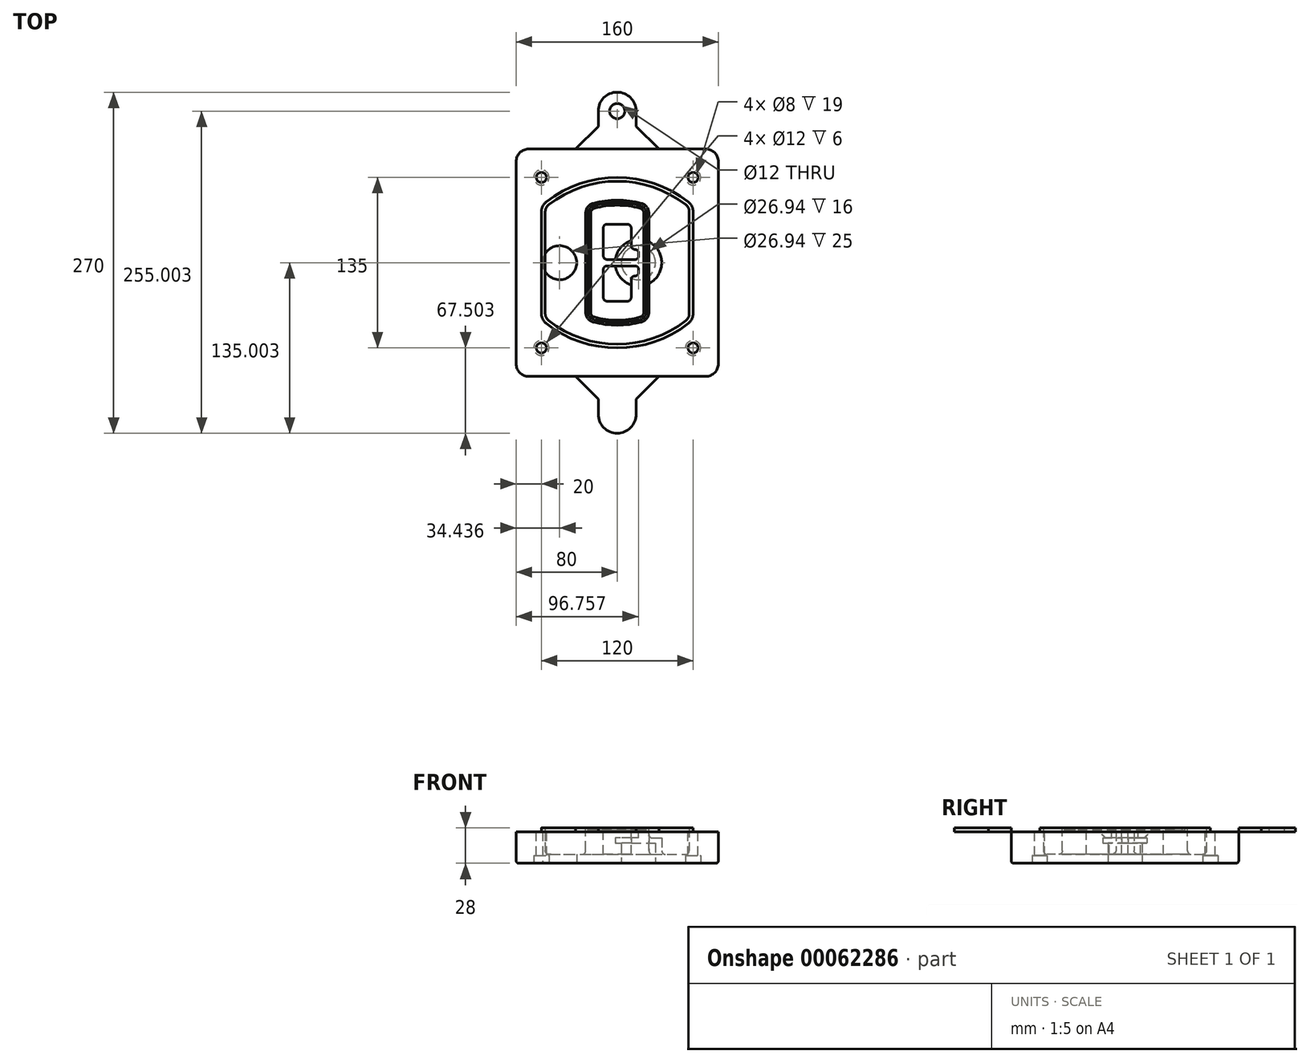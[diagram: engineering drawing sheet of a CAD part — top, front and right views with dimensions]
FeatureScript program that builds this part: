
annotation { "Feature Type Name" : "Feature", "Feature Type Description" : "" }
export const myFeature = defineFeature(function(context is Context, id is Id, definition is map)
    precondition{}
    {
        {
            var Q0;
            Q0=qCreatedBy(makeId("Top.planeOp"),FACE);
            var sketch = newSketch(context, id + "F0", { "sketchPlane" : qUnion([Q0])});
            skPoint(sketch, "E0.rect.middle", {"position": v(0, 0) * mm});
            skLineSegment(sketch, "E1.bottom", {"start": v(24.05, 28.38) * mm, "end": v(164.05, 28.38) * mm});
            skLineSegment(sketch, "E1.top", {"start": v(24.05, 208.38) * mm, "end": v(164.05, 208.38) * mm});
            skLineSegment(sketch, "E1.left", {"start": v(14.05, 38.38) * mm, "end": v(14.05, 198.38) * mm});
            skLineSegment(sketch, "E1.right", {"start": v(174.05, 38.38) * mm, "end": v(174.05, 198.38) * mm});
            skLineSegment(sketch, "E2", {"start": v(14.05, 208.38) * mm, "end": v(174.05, 28.38) * mm, "construction": true});
            skLineSegment(sketch, "E3", {"start": v(174.05, 208.38) * mm, "end": v(14.05, 28.38) * mm, "construction": true});
            skCircle(sketch, "E4", {"center": v(34.05, 185.88) * mm, "radius": 4 * mm});
            skCircle(sketch, "E5", {"center": v(154.05, 185.88) * mm, "radius": 4 * mm});
            skCircle(sketch, "E6", {"center": v(154.05, 50.88) * mm, "radius": 4 * mm});
            skCircle(sketch, "E7", {"center": v(34.05, 50.88) * mm, "radius": 4 * mm});
            skLineSegment(sketch, "E8", {"start": v(34.05, 185.88) * mm, "end": v(154.05, 185.88) * mm, "construction": true});
            skLineSegment(sketch, "E9", {"start": v(154.05, 185.88) * mm, "end": v(154.05, 50.88) * mm, "construction": true});
            skLineSegment(sketch, "E10", {"start": v(154.05, 50.88) * mm, "end": v(34.05, 50.88) * mm, "construction": true});
            skLineSegment(sketch, "E11", {"start": v(34.05, 50.88) * mm, "end": v(34.05, 185.88) * mm, "construction": true});
            skLineSegment(sketch, "E12", {"start": v(34.05, 158.68) * mm, "end": v(34.05, 78.09) * mm});
            skLineSegment(sketch, "E13", {"start": v(154.05, 158.68) * mm, "end": v(154.05, 78.09) * mm});
            skArc(sketch, "E14", {"start": v(150.2, 166.56) * mm, "mid": v(94.05, 185.88) * mm, "end": v(37.9, 166.56) * mm});
            skArc(sketch, "E15", {"start": v(37.9, 70.2) * mm, "mid": v(94.05, 50.88) * mm, "end": v(150.2, 70.2) * mm});
            skLineSegment(sketch, "E16", {"start": v(34.05, 118.38) * mm, "end": v(154.05, 118.38) * mm, "construction": true});
            skPoint(sketch, "E17.visualSharp", {"position": v(34.05, 73.38) * mm});
            skArc(sketch, "E17.filletArc", {"start": v(34.05, 78.09) * mm, "mid": v(35.06, 73.7) * mm, "end": v(37.9, 70.2) * mm});
            skPoint(sketch, "E18.visualSharp", {"position": v(34.05, 163.38) * mm});
            skArc(sketch, "E18.filletArc", {"start": v(37.9, 166.56) * mm, "mid": v(35.06, 163.06) * mm, "end": v(34.05, 158.68) * mm});
            skPoint(sketch, "E19.visualSharp", {"position": v(154.05, 163.38) * mm});
            skArc(sketch, "E19.filletArc", {"start": v(154.05, 158.68) * mm, "mid": v(153.04, 163.06) * mm, "end": v(150.2, 166.56) * mm});
            skPoint(sketch, "E20.visualSharp", {"position": v(154.05, 73.38) * mm});
            skArc(sketch, "E20.filletArc", {"start": v(150.2, 70.2) * mm, "mid": v(153.04, 73.7) * mm, "end": v(154.05, 78.09) * mm});
            skPoint(sketch, "E21.visualSharp", {"position": v(14.05, 208.38) * mm});
            skArc(sketch, "E21.filletArc", {"start": v(24.05, 208.38) * mm, "mid": v(16.98, 205.45) * mm, "end": v(14.05, 198.38) * mm});
            skPoint(sketch, "E22.visualSharp", {"position": v(174.05, 208.38) * mm});
            skArc(sketch, "E22.filletArc", {"start": v(174.05, 198.38) * mm, "mid": v(171.12, 205.45) * mm, "end": v(164.05, 208.38) * mm});
            skPoint(sketch, "E23.visualSharp", {"position": v(174.05, 28.38) * mm});
            skArc(sketch, "E23.filletArc", {"start": v(164.05, 28.38) * mm, "mid": v(171.12, 31.31) * mm, "end": v(174.05, 38.38) * mm});
            skPoint(sketch, "E24.visualSharp", {"position": v(14.05, 28.38) * mm});
            skArc(sketch, "E24.filletArc", {"start": v(14.05, 38.38) * mm, "mid": v(16.98, 31.31) * mm, "end": v(24.05, 28.38) * mm});
            skArc(sketch, "E25.0", {"start": v(151.05, 158.68) * mm, "mid": v(150.34, 161.75) * mm, "end": v(148.36, 164.2) * mm});
            skLineSegment(sketch, "E25.1", {"start": v(151.05, 158.68) * mm, "end": v(151.05, 78.09) * mm});
            skArc(sketch, "E25.2", {"start": v(148.36, 72.57) * mm, "mid": v(150.34, 75.02) * mm, "end": v(151.05, 78.09) * mm});
            skArc(sketch, "E25.3", {"start": v(39.74, 72.57) * mm, "mid": v(94.05, 53.88) * mm, "end": v(148.36, 72.57) * mm});
            skArc(sketch, "E25.4", {"start": v(37.05, 78.09) * mm, "mid": v(37.76, 75.02) * mm, "end": v(39.74, 72.57) * mm});
            skArc(sketch, "E25.5", {"start": v(148.36, 164.2) * mm, "mid": v(94.05, 182.88) * mm, "end": v(39.74, 164.2) * mm});
            skLineSegment(sketch, "E25.6", {"start": v(37.05, 158.68) * mm, "end": v(37.05, 78.09) * mm});
            skArc(sketch, "E25.7", {"start": v(39.74, 164.2) * mm, "mid": v(37.76, 161.75) * mm, "end": v(37.05, 158.68) * mm});
            skArc(sketch, "E26.0", {"start": v(35.43, 169.71) * mm, "mid": v(31.47, 164.82) * mm, "end": v(30.05, 158.68) * mm});
            skArc(sketch, "E26.1", {"start": v(152.67, 169.71) * mm, "mid": v(94.05, 189.88) * mm, "end": v(35.43, 169.71) * mm});
            skArc(sketch, "E26.2", {"start": v(158.05, 158.68) * mm, "mid": v(156.63, 164.82) * mm, "end": v(152.67, 169.71) * mm});
            skLineSegment(sketch, "E26.3", {"start": v(158.05, 158.68) * mm, "end": v(158.05, 78.09) * mm});
            skArc(sketch, "E26.4", {"start": v(152.67, 67.05) * mm, "mid": v(156.63, 71.95) * mm, "end": v(158.05, 78.09) * mm});
            skLineSegment(sketch, "E26.5", {"start": v(30.05, 158.68) * mm, "end": v(30.05, 78.09) * mm});
            skArc(sketch, "E26.6", {"start": v(35.43, 67.05) * mm, "mid": v(94.05, 46.88) * mm, "end": v(152.67, 67.05) * mm});
            skArc(sketch, "E26.7", {"start": v(30.05, 78.09) * mm, "mid": v(31.47, 71.95) * mm, "end": v(35.43, 67.05) * mm});
            skSolve(sketch);
        }
        {
            var Q0;
            Q0=makeQuery(id+"F0.imprint","IMPRINT",FACE,{"disambiguationData":[TD([[makeQuery(id+"F0.imprint","IMPRINT",EDGE,{"derivedFrom":sQuery(id+"F0.wireOp",EDGE,"E1.bottom")}),1.0]])]});
            var Q1;
            Q1=makeQuery(id+"F0.imprint","IMPRINT",FACE,{"disambiguationData":[TD([[makeQuery(id+"F0.imprint","IMPRINT",EDGE,{"derivedFrom":sQuery(id+"F0.wireOp",EDGE,"E12")}),1.0]])]});
            var Q2;
            Q2=makeQuery(id+"F0.imprint","IMPRINT",FACE,{"disambiguationData":[TD([[makeQuery(id+"F0.imprint","IMPRINT",EDGE,{"derivedFrom":sQuery(id+"F0.wireOp",EDGE,"E25.0")}),1.0]])]});
            var Q3;
            Q3=makeQuery(id+"F0.imprint","IMPRINT",FACE,{"disambiguationData":[TD([[makeQuery(id+"F0.imprint","IMPRINT",EDGE,{"derivedFrom":sQuery(id+"F0.wireOp",EDGE,"E12")}),-1.0]])]});
            extrude(context, id + "F1", {"entities" : qUnion([Q0, Q1, Q2, Q3]), "oppositeDirection" : true, "depth" : 25 * mm});
        }
        {
            var Q0;
            Q0=makeQuery(id+"F0.imprint","IMPRINT",FACE,{"disambiguationData":[TD([[makeQuery(id+"F0.imprint","IMPRINT",EDGE,{"derivedFrom":sQuery(id+"F0.wireOp",EDGE,"E12")}),1.0]])]});
            extrude(context, id + "F2", {"entities" : qUnion([Q0]), "operationType" : NewBodyOperationType.ADD, "depth" : 3 * mm});
        }
        {
            var Q0;
            Q0=makeQuery(id+"F0.imprint","IMPRINT",FACE,{"disambiguationData":[TD([[makeQuery(id+"F0.imprint","IMPRINT",EDGE,{"derivedFrom":sQuery(id+"F0.wireOp",EDGE,"E25.0")}),1.0]])]});
            extrude(context, id + "F3", {"entities" : qUnion([Q0]), "operationType" : NewBodyOperationType.REMOVE, "oppositeDirection" : true, "depth" : 18 * mm});
        }
        {
            var Q0;
            Q0=makeQuery(id+"F2.opExtrude","CAP_FACE",FACE,{"disambiguationData":[OSD([sQuery(id+"F0.wireOp",EDGE,"E12"),sQuery(id+"F0.wireOp",EDGE,"E13"),sQuery(id+"F0.wireOp",EDGE,"E14"),sQuery(id+"F0.wireOp",EDGE,"E15"),sQuery(id+"F0.wireOp",EDGE,"E17.filletArc"),sQuery(id+"F0.wireOp",EDGE,"E18.filletArc"),sQuery(id+"F0.wireOp",EDGE,"E19.filletArc"),sQuery(id+"F0.wireOp",EDGE,"E20.filletArc"),sQuery(id+"F0.wireOp",EDGE,"E25.0"),sQuery(id+"F0.wireOp",EDGE,"E25.1"),sQuery(id+"F0.wireOp",EDGE,"E25.2"),sQuery(id+"F0.wireOp",EDGE,"E25.3"),sQuery(id+"F0.wireOp",EDGE,"E25.4"),sQuery(id+"F0.wireOp",EDGE,"E25.5"),sQuery(id+"F0.wireOp",EDGE,"E25.6"),sQuery(id+"F0.wireOp",EDGE,"E25.7")])],"isStart":false});
            var sketch = newSketch(context, id + "F4", { "sketchPlane" : qUnion([Q0])});
            skArc(sketch, "E27.0", {"start": v(74.97, 71.41) * mm, "mid": v(94.05, 68.88) * mm, "end": v(113.13, 71.41) * mm});
            skArc(sketch, "E28.0", {"start": v(113.13, 165.35) * mm, "mid": v(94.05, 167.88) * mm, "end": v(74.97, 165.35) * mm});
            skLineSegment(sketch, "E29", {"start": v(69.05, 157.63) * mm, "end": v(69.05, 79.14) * mm});
            skLineSegment(sketch, "E30", {"start": v(119.05, 157.63) * mm, "end": v(119.05, 79.14) * mm});
            skLineSegment(sketch, "E31", {"start": v(69.05, 163.48) * mm, "end": v(119.05, 163.48) * mm, "construction": true});
            skLineSegment(sketch, "E32", {"start": v(69.05, 73.28) * mm, "end": v(119.05, 73.28) * mm, "construction": true});
            skPoint(sketch, "E33.visualSharp", {"position": v(69.05, 163.48) * mm});
            skArc(sketch, "E33.filletArc", {"start": v(74.97, 165.35) * mm, "mid": v(70.7, 162.5) * mm, "end": v(69.05, 157.63) * mm});
            skPoint(sketch, "E34.visualSharp", {"position": v(119.05, 163.48) * mm});
            skArc(sketch, "E34.filletArc", {"start": v(119.05, 157.63) * mm, "mid": v(117.4, 162.5) * mm, "end": v(113.13, 165.35) * mm});
            skPoint(sketch, "E35.visualSharp", {"position": v(119.05, 73.28) * mm});
            skArc(sketch, "E35.filletArc", {"start": v(113.13, 71.41) * mm, "mid": v(117.4, 74.27) * mm, "end": v(119.05, 79.14) * mm});
            skPoint(sketch, "E36.visualSharp", {"position": v(69.05, 73.28) * mm});
            skArc(sketch, "E36.filletArc", {"start": v(69.05, 79.14) * mm, "mid": v(70.7, 74.27) * mm, "end": v(74.97, 71.41) * mm});
            skArc(sketch, "E37.0", {"start": v(148.36, 164.2) * mm, "mid": v(94.05, 182.88) * mm, "end": v(39.74, 164.2) * mm});
            skArc(sketch, "E37.1", {"start": v(39.74, 164.2) * mm, "mid": v(37.76, 161.75) * mm, "end": v(37.05, 158.68) * mm});
            skLineSegment(sketch, "E37.2", {"start": v(37.05, 158.68) * mm, "end": v(37.05, 78.09) * mm});
            skArc(sketch, "E37.3", {"start": v(37.05, 78.09) * mm, "mid": v(37.76, 75.02) * mm, "end": v(39.74, 72.57) * mm});
            skArc(sketch, "E37.4", {"start": v(39.74, 72.57) * mm, "mid": v(94.05, 53.88) * mm, "end": v(148.36, 72.57) * mm});
            skArc(sketch, "E37.5", {"start": v(148.36, 72.57) * mm, "mid": v(150.34, 75.02) * mm, "end": v(151.05, 78.09) * mm});
            skLineSegment(sketch, "E37.6", {"start": v(151.05, 158.68) * mm, "end": v(151.05, 78.09) * mm});
            skArc(sketch, "E37.7", {"start": v(151.05, 158.68) * mm, "mid": v(150.34, 161.75) * mm, "end": v(148.36, 164.2) * mm});
            skLineSegment(sketch, "E38.0", {"start": v(117.05, 157.63) * mm, "end": v(117.05, 79.14) * mm});
            skArc(sketch, "E38.1", {"start": v(112.61, 73.34) * mm, "mid": v(115.81, 75.49) * mm, "end": v(117.05, 79.14) * mm});
            skArc(sketch, "E38.2", {"start": v(75.49, 73.34) * mm, "mid": v(94.05, 70.88) * mm, "end": v(112.61, 73.34) * mm});
            skArc(sketch, "E38.3", {"start": v(71.05, 79.14) * mm, "mid": v(72.29, 75.49) * mm, "end": v(75.49, 73.34) * mm});
            skLineSegment(sketch, "E38.4", {"start": v(71.05, 157.63) * mm, "end": v(71.05, 79.14) * mm});
            skArc(sketch, "E38.5", {"start": v(117.05, 157.63) * mm, "mid": v(115.81, 161.28) * mm, "end": v(112.61, 163.42) * mm});
            skArc(sketch, "E38.6", {"start": v(75.49, 163.42) * mm, "mid": v(72.29, 161.28) * mm, "end": v(71.05, 157.63) * mm});
            skArc(sketch, "E38.7", {"start": v(112.61, 163.42) * mm, "mid": v(94.05, 165.88) * mm, "end": v(75.49, 163.42) * mm});
            skArc(sketch, "E39.0", {"start": v(115.05, 157.63) * mm, "mid": v(114.23, 160.06) * mm, "end": v(112.1, 161.5) * mm});
            skLineSegment(sketch, "E39.1", {"start": v(115.05, 157.63) * mm, "end": v(115.05, 79.14) * mm});
            skArc(sketch, "E39.2", {"start": v(112.1, 75.27) * mm, "mid": v(114.23, 76.7) * mm, "end": v(115.05, 79.14) * mm});
            skArc(sketch, "E39.3", {"start": v(76, 75.27) * mm, "mid": v(94.05, 72.88) * mm, "end": v(112.1, 75.27) * mm});
            skArc(sketch, "E39.4", {"start": v(73.05, 79.14) * mm, "mid": v(73.87, 76.7) * mm, "end": v(76, 75.27) * mm});
            skArc(sketch, "E39.5", {"start": v(112.1, 161.5) * mm, "mid": v(94.05, 163.88) * mm, "end": v(76, 161.5) * mm});
            skLineSegment(sketch, "E39.6", {"start": v(73.05, 157.63) * mm, "end": v(73.05, 79.14) * mm});
            skArc(sketch, "E39.7", {"start": v(76, 161.5) * mm, "mid": v(73.87, 160.06) * mm, "end": v(73.05, 157.63) * mm});
            skLineSegment(sketch, "E40", {"start": v(69.05, 118.38) * mm, "end": v(119.05, 118.38) * mm, "construction": true});
            skLineSegment(sketch, "E41", {"start": v(83.05, 123.88) * mm, "end": v(83.05, 145.88) * mm});
            skLineSegment(sketch, "E42", {"start": v(86.05, 148.88) * mm, "end": v(102.05, 148.88) * mm});
            skLineSegment(sketch, "E43", {"start": v(105.05, 145.88) * mm, "end": v(105.05, 131.88) * mm});
            skLineSegment(sketch, "E44", {"start": v(108.05, 128.88) * mm, "end": v(108.05, 128.88) * mm});
            skLineSegment(sketch, "E45", {"start": v(111.05, 125.88) * mm, "end": v(111.05, 123.88) * mm});
            skLineSegment(sketch, "E46", {"start": v(108.05, 120.88) * mm, "end": v(86.05, 120.88) * mm});
            skPoint(sketch, "E47.visualSharp", {"position": v(83.05, 148.88) * mm});
            skArc(sketch, "E47.filletArc", {"start": v(86.05, 148.88) * mm, "mid": v(83.93, 148) * mm, "end": v(83.05, 145.88) * mm});
            skPoint(sketch, "E48.visualSharp", {"position": v(105.05, 148.88) * mm});
            skArc(sketch, "E48.filletArc", {"start": v(105.05, 145.88) * mm, "mid": v(104.17, 148) * mm, "end": v(102.05, 148.88) * mm});
            skPoint(sketch, "E49.visualSharp", {"position": v(105.05, 128.88) * mm});
            skArc(sketch, "E49.filletArc", {"start": v(105.05, 131.88) * mm, "mid": v(105.93, 129.76) * mm, "end": v(108.05, 128.88) * mm});
            skPoint(sketch, "E50.visualSharp", {"position": v(111.05, 128.88) * mm});
            skArc(sketch, "E50.filletArc", {"start": v(111.05, 125.88) * mm, "mid": v(110.17, 128) * mm, "end": v(108.05, 128.88) * mm});
            skPoint(sketch, "E51.visualSharp", {"position": v(111.05, 120.88) * mm});
            skArc(sketch, "E51.filletArc", {"start": v(108.05, 120.88) * mm, "mid": v(110.17, 121.76) * mm, "end": v(111.05, 123.88) * mm});
            skPoint(sketch, "E52.visualSharp", {"position": v(83.05, 120.88) * mm});
            skArc(sketch, "E52.filletArc", {"start": v(83.05, 123.88) * mm, "mid": v(83.93, 121.76) * mm, "end": v(86.05, 120.88) * mm});
            skLineSegment(sketch, "E53.0.MirrorCS", {"start": v(108.05, 115.88) * mm, "end": v(86.05, 115.88) * mm});
            skArc(sketch, "E54.0.MirrorCS", {"start": v(83.05, 112.88) * mm, "mid": v(83.93, 115) * mm, "end": v(86.05, 115.88) * mm});
            skLineSegment(sketch, "E55.0.MirrorCS", {"start": v(83.05, 112.88) * mm, "end": v(83.05, 90.88) * mm});
            skArc(sketch, "E56.0.MirrorCS", {"start": v(86.05, 87.88) * mm, "mid": v(83.93, 88.76) * mm, "end": v(83.05, 90.88) * mm});
            skLineSegment(sketch, "E57.0.MirrorCS", {"start": v(86.05, 87.88) * mm, "end": v(102.05, 87.88) * mm});
            skArc(sketch, "E58.0.MirrorCS", {"start": v(105.05, 90.88) * mm, "mid": v(104.17, 88.76) * mm, "end": v(102.05, 87.88) * mm});
            skLineSegment(sketch, "E59.0.MirrorCS", {"start": v(105.05, 90.88) * mm, "end": v(105.05, 104.88) * mm});
            skArc(sketch, "E60.0.MirrorCS", {"start": v(105.05, 104.88) * mm, "mid": v(105.93, 107) * mm, "end": v(108.05, 107.88) * mm});
            skArc(sketch, "E61.0.MirrorCS", {"start": v(111.05, 110.88) * mm, "mid": v(110.17, 108.76) * mm, "end": v(108.05, 107.88) * mm});
            skLineSegment(sketch, "E62.0.MirrorCS", {"start": v(111.05, 110.88) * mm, "end": v(111.05, 112.88) * mm});
            skArc(sketch, "E63.0.MirrorCS", {"start": v(108.05, 115.88) * mm, "mid": v(110.17, 115) * mm, "end": v(111.05, 112.88) * mm});
            skSolve(sketch);
        }
        {
            var Q0;
            Q0=makeQuery(id+"F4.imprint","IMPRINT",FACE,{"disambiguationData":[TD([[makeQuery(id+"F4.imprint","IMPRINT",EDGE,{"derivedFrom":sQuery(id+"F4.wireOp",EDGE,"E27.0")}),1.0]])]});
            var Q1;
            Q1=makeQuery(id+"F4.imprint","IMPRINT",FACE,{"disambiguationData":[TD([[makeQuery(id+"F4.imprint","IMPRINT",EDGE,{"derivedFrom":sQuery(id+"F4.wireOp",EDGE,"E38.0")}),-1.0]])]});
            var Q2;
            Q2=makeQuery(id+"F4.imprint","IMPRINT",FACE,{"disambiguationData":[TD([[makeQuery(id+"F4.imprint","IMPRINT",EDGE,{"derivedFrom":sQuery(id+"F4.wireOp",EDGE,"E39.0")}),1.0]])]});
            extrude(context, id + "F5", {"entities" : qUnion([Q0, Q1, Q2]), "operationType" : NewBodyOperationType.ADD, "endBound" : BoundingType.UP_TO_NEXT, "oppositeDirection" : true, "depth" : 25 * mm});
        }
        {
            var Q0;
            Q0=makeQuery(id+"F4.imprint","IMPRINT",FACE,{"disambiguationData":[TD([[makeQuery(id+"F4.imprint","IMPRINT",EDGE,{"derivedFrom":sQuery(id+"F4.wireOp",EDGE,"E38.0")}),-1.0]])]});
            extrude(context, id + "F6", {"entities" : qUnion([Q0]), "operationType" : NewBodyOperationType.REMOVE, "oppositeDirection" : true, "depth" : 2 * mm});
        }
        {
            var Q0;
            Q0=makeQuery(id+"F1.opExtrude","CAP_FACE",FACE,{"disambiguationData":[OSD([sQuery(id+"F0.wireOp",EDGE,"E1.bottom"),sQuery(id+"F0.wireOp",EDGE,"E1.top"),sQuery(id+"F0.wireOp",EDGE,"E1.left"),sQuery(id+"F0.wireOp",EDGE,"E1.right"),sQuery(id+"F0.wireOp",EDGE,"E4"),sQuery(id+"F0.wireOp",EDGE,"E5"),sQuery(id+"F0.wireOp",EDGE,"E6"),sQuery(id+"F0.wireOp",EDGE,"E7"),sQuery(id+"F0.wireOp",EDGE,"E21.filletArc"),sQuery(id+"F0.wireOp",EDGE,"E22.filletArc"),sQuery(id+"F0.wireOp",EDGE,"E23.filletArc"),sQuery(id+"F0.wireOp",EDGE,"E24.filletArc")])],"isStart":false});
            var sketch = newSketch(context, id + "F7", { "sketchPlane" : qUnion([Q0])});
            skCircle(sketch, "E64", {"center": v(110.8, -118.38) * mm, "radius": 13.47 * mm});
            skCircle(sketch, "E65", {"center": v(48.49, -118.38) * mm, "radius": 13.47 * mm});
            skLineSegment(sketch, "E66", {"start": v(174.05, -118.38) * mm, "end": v(14.05, -118.38) * mm});
            skCircle(sketch, "E67", {"center": v(110.8, -118.38) * mm, "radius": 18.47 * mm});
            skCircle(sketch, "E68", {"center": v(154.05, -185.88) * mm, "radius": 6 * mm});
            skCircle(sketch, "E69", {"center": v(34.05, -185.88) * mm, "radius": 6 * mm});
            skCircle(sketch, "E70", {"center": v(34.05, -50.88) * mm, "radius": 6 * mm});
            skCircle(sketch, "E71", {"center": v(154.05, -50.88) * mm, "radius": 6 * mm});
            skSolve(sketch);
        }
        {
            var Q0;
            {var subQ1=sQuery(id+"F7.wireOp",EDGE,"E66");var subQ4=sQuery(id+"F7.wireOp",EDGE,"E64");var subQ6=makeQuery(id+"F7.imprint","INTERSECT",VERTEX,{"disambiguationData":[OD(0.0)],"derivedFrom":[subQ4,subQ1]});Q0=makeQuery(id+"F7.imprint","IMPRINT",FACE,{"disambiguationData":[TD([[makeQuery(id+"F7.imprint","IMPRINT",EDGE,{"disambiguationData":[TD([[subQ6,-1.0]])],"derivedFrom":subQ4}),-1.0]])]});}
            var Q1;
            {var subQ0=sQuery(id+"F7.wireOp",EDGE,"E66");var subQ1=sQuery(id+"F7.wireOp",EDGE,"E64");var subQ3=makeQuery(id+"F7.imprint","INTERSECT",VERTEX,{"disambiguationData":[OD(0.0)],"derivedFrom":[subQ1,subQ0]});Q1=makeQuery(id+"F7.imprint","IMPRINT",FACE,{"disambiguationData":[TD([[makeQuery(id+"F7.imprint","IMPRINT",EDGE,{"disambiguationData":[TD([[subQ3,-1.0]])],"derivedFrom":subQ1}),1.0]])]});}
            var Q2;
            {var subQ0=sQuery(id+"F7.wireOp",EDGE,"E66");var subQ1=sQuery(id+"F7.wireOp",EDGE,"E64");var subQ3=makeQuery(id+"F7.imprint","INTERSECT",VERTEX,{"disambiguationData":[OD(0.0)],"derivedFrom":[subQ1,subQ0]});Q2=makeQuery(id+"F7.imprint","IMPRINT",FACE,{"disambiguationData":[TD([[makeQuery(id+"F7.imprint","IMPRINT",EDGE,{"disambiguationData":[TD([[subQ3,1.0]])],"derivedFrom":subQ1}),1.0]])]});}
            var Q3;
            {var subQ1=sQuery(id+"F7.wireOp",EDGE,"E66");var subQ4=sQuery(id+"F7.wireOp",EDGE,"E64");var subQ6=makeQuery(id+"F7.imprint","INTERSECT",VERTEX,{"disambiguationData":[OD(0.0)],"derivedFrom":[subQ4,subQ1]});Q3=makeQuery(id+"F7.imprint","IMPRINT",FACE,{"disambiguationData":[TD([[makeQuery(id+"F7.imprint","IMPRINT",EDGE,{"disambiguationData":[TD([[subQ6,1.0]])],"derivedFrom":subQ4}),-1.0]])]});}
            extrude(context, id + "F8", {"entities" : qUnion([Q0, Q1, Q2, Q3]), "operationType" : NewBodyOperationType.ADD, "oppositeDirection" : true, "depth" : 20 * mm});
        }
        {
            var Q0;
            {var subQ0=sQuery(id+"F7.wireOp",EDGE,"E66");var subQ1=sQuery(id+"F7.wireOp",EDGE,"E64");var subQ3=makeQuery(id+"F7.imprint","INTERSECT",VERTEX,{"disambiguationData":[OD(0.0)],"derivedFrom":[subQ1,subQ0]});Q0=makeQuery(id+"F7.imprint","IMPRINT",FACE,{"disambiguationData":[TD([[makeQuery(id+"F7.imprint","IMPRINT",EDGE,{"disambiguationData":[TD([[subQ3,-1.0]])],"derivedFrom":subQ1}),1.0]])]});}
            var Q1;
            {var subQ0=sQuery(id+"F7.wireOp",EDGE,"E66");var subQ1=sQuery(id+"F7.wireOp",EDGE,"E64");var subQ3=makeQuery(id+"F7.imprint","INTERSECT",VERTEX,{"disambiguationData":[OD(0.0)],"derivedFrom":[subQ1,subQ0]});Q1=makeQuery(id+"F7.imprint","IMPRINT",FACE,{"disambiguationData":[TD([[makeQuery(id+"F7.imprint","IMPRINT",EDGE,{"disambiguationData":[TD([[subQ3,1.0]])],"derivedFrom":subQ1}),1.0]])]});}
            extrude(context, id + "F9", {"entities" : qUnion([Q0, Q1]), "operationType" : NewBodyOperationType.REMOVE, "oppositeDirection" : true, "depth" : 16 * mm});
        }
        {
            var Q0;
            {var subQ0=sQuery(id+"F7.wireOp",EDGE,"E66");var subQ1=sQuery(id+"F7.wireOp",EDGE,"E65");var subQ3=makeQuery(id+"F7.imprint","INTERSECT",VERTEX,{"disambiguationData":[OD(0.0)],"derivedFrom":[subQ1,subQ0]});Q0=makeQuery(id+"F7.imprint","IMPRINT",FACE,{"disambiguationData":[TD([[makeQuery(id+"F7.imprint","IMPRINT",EDGE,{"disambiguationData":[TD([[subQ3,-1.0]])],"derivedFrom":subQ1}),1.0]])]});}
            var Q1;
            {var subQ0=sQuery(id+"F7.wireOp",EDGE,"E66");var subQ1=sQuery(id+"F7.wireOp",EDGE,"E65");var subQ3=makeQuery(id+"F7.imprint","INTERSECT",VERTEX,{"disambiguationData":[OD(0.0)],"derivedFrom":[subQ1,subQ0]});Q1=makeQuery(id+"F7.imprint","IMPRINT",FACE,{"disambiguationData":[TD([[makeQuery(id+"F7.imprint","IMPRINT",EDGE,{"disambiguationData":[TD([[subQ3,1.0]])],"derivedFrom":subQ1}),1.0]])]});}
            extrude(context, id + "F10", {"entities" : qUnion([Q0, Q1]), "operationType" : NewBodyOperationType.REMOVE, "oppositeDirection" : true, "depth" : 25 * mm});
        }
        {
            var Q0;
            Q0=makeQuery(id+"F7.imprint","IMPRINT",FACE,{"disambiguationData":[TD([[makeQuery(id+"F7.imprint","IMPRINT",EDGE,{"derivedFrom":sQuery(id+"F7.wireOp",EDGE,"E68")}),1.0]])]});
            var Q1;
            Q1=makeQuery(id+"F7.imprint","IMPRINT",FACE,{"disambiguationData":[TD([[makeQuery(id+"F7.imprint","IMPRINT",EDGE,{"derivedFrom":makeQuery(id+"F1.opExtrude","CAP_EDGE",EDGE,{"disambiguationData":[OSD([sQuery(id+"F0.wireOp",EDGE,"E5")])],"isStart":false})}),-1.0]])]});
            var Q2;
            Q2=makeQuery(id+"F7.imprint","IMPRINT",FACE,{"disambiguationData":[TD([[makeQuery(id+"F7.imprint","IMPRINT",EDGE,{"derivedFrom":sQuery(id+"F7.wireOp",EDGE,"E69")}),1.0]])]});
            var Q3;
            Q3=makeQuery(id+"F7.imprint","IMPRINT",FACE,{"disambiguationData":[TD([[makeQuery(id+"F7.imprint","IMPRINT",EDGE,{"derivedFrom":makeQuery(id+"F1.opExtrude","CAP_EDGE",EDGE,{"disambiguationData":[OSD([sQuery(id+"F0.wireOp",EDGE,"E4")])],"isStart":false})}),-1.0]])]});
            var Q4;
            Q4=makeQuery(id+"F7.imprint","IMPRINT",FACE,{"disambiguationData":[TD([[makeQuery(id+"F7.imprint","IMPRINT",EDGE,{"derivedFrom":sQuery(id+"F7.wireOp",EDGE,"E70")}),1.0]])]});
            var Q5;
            Q5=makeQuery(id+"F7.imprint","IMPRINT",FACE,{"disambiguationData":[TD([[makeQuery(id+"F7.imprint","IMPRINT",EDGE,{"derivedFrom":makeQuery(id+"F1.opExtrude","CAP_EDGE",EDGE,{"disambiguationData":[OSD([sQuery(id+"F0.wireOp",EDGE,"E7")])],"isStart":false})}),-1.0]])]});
            var Q6;
            Q6=makeQuery(id+"F7.imprint","IMPRINT",FACE,{"disambiguationData":[TD([[makeQuery(id+"F7.imprint","IMPRINT",EDGE,{"derivedFrom":sQuery(id+"F7.wireOp",EDGE,"E71")}),1.0]])]});
            var Q7;
            Q7=makeQuery(id+"F7.imprint","IMPRINT",FACE,{"disambiguationData":[TD([[makeQuery(id+"F7.imprint","IMPRINT",EDGE,{"derivedFrom":makeQuery(id+"F1.opExtrude","CAP_EDGE",EDGE,{"disambiguationData":[OSD([sQuery(id+"F0.wireOp",EDGE,"E6")])],"isStart":false})}),-1.0]])]});
            extrude(context, id + "F11", {"entities" : qUnion([Q0, Q1, Q2, Q3, Q4, Q5, Q6, Q7]), "operationType" : NewBodyOperationType.REMOVE, "oppositeDirection" : true, "depth" : 6 * mm});
        }
        {
            var Q0;
            Q0=makeQuery(id+"F9.boolean.opBoolean","COPY",FACE,{"derivedFrom":makeQuery(id+"F9.opExtrude","CAP_FACE",FACE,{"disambiguationData":[OSD([sQuery(id+"F7.wireOp",EDGE,"E64")])],"isStart":false})});
            var sketch = newSketch(context, id + "F12", { "sketchPlane" : qUnion([Q0])});
            skArc(sketch, "E72.0", {"start": v(105.05, -100.83) * mm, "mid": v(96.62, -106.56) * mm, "end": v(92.5, -115.88) * mm});
            skArc(sketch, "E72.1", {"start": v(92.5, -120.88) * mm, "mid": v(96.62, -130.2) * mm, "end": v(105.05, -135.93) * mm});
            skLineSegment(sketch, "E73", {"start": v(92.5, -120.88) * mm, "end": v(108.05, -120.88) * mm});
            skLineSegment(sketch, "E74.0", {"start": v(108.05, -115.88) * mm, "end": v(92.5, -115.88) * mm});
            skArc(sketch, "E74.1", {"start": v(108.05, -115.88) * mm, "mid": v(110.17, -115) * mm, "end": v(111.05, -112.88) * mm});
            skLineSegment(sketch, "E74.2", {"start": v(111.05, -110.88) * mm, "end": v(111.05, -112.88) * mm});
            skArc(sketch, "E74.3", {"start": v(111.05, -110.88) * mm, "mid": v(110.17, -108.76) * mm, "end": v(108.05, -107.88) * mm});
            skArc(sketch, "E74.4", {"start": v(105.05, -104.88) * mm, "mid": v(105.93, -107) * mm, "end": v(108.05, -107.88) * mm});
            skLineSegment(sketch, "E74.5", {"start": v(105.05, -100.83) * mm, "end": v(105.05, -104.88) * mm});
            skLineSegment(sketch, "E74.7", {"start": v(108.05, -120.88) * mm, "end": v(92.5, -120.88) * mm});
            skArc(sketch, "E74.8", {"start": v(108.05, -120.88) * mm, "mid": v(110.17, -121.76) * mm, "end": v(111.05, -123.88) * mm});
            skLineSegment(sketch, "E74.9", {"start": v(111.05, -125.88) * mm, "end": v(111.05, -123.88) * mm});
            skArc(sketch, "E74.10", {"start": v(111.05, -125.88) * mm, "mid": v(110.17, -128) * mm, "end": v(108.05, -128.88) * mm});
            skArc(sketch, "E74.11", {"start": v(105.05, -131.88) * mm, "mid": v(105.93, -129.76) * mm, "end": v(108.05, -128.88) * mm});
            skLineSegment(sketch, "E74.12", {"start": v(105.05, -135.93) * mm, "end": v(105.05, -131.88) * mm});
            skPoint(sketch, "E75.orphan", {"position": v(105.05, -145.88) * mm});
            skPoint(sketch, "E76.orphan", {"position": v(86.05, -120.88) * mm});
            skPoint(sketch, "E77.orphan", {"position": v(86.05, -115.88) * mm});
            skPoint(sketch, "E78.orphan", {"position": v(105.05, -90.88) * mm});
            skSolve(sketch);
        }
        {
            var Q0;
            {var subQ7=sQuery(id+"F12.wireOp",EDGE,"E72.0");var subQ14=sQuery(id+"F12.wireOp",EDGE,"E72.1");var subQ16=sQuery(id+"F12.wireOp",EDGE,"E74.1");var subQ18=sQuery(id+"F12.wireOp",EDGE,"E74.8");Q0=qUnion([makeQuery(id+"F12.imprint","IMPRINT",FACE,{"disambiguationData":[TD([[makeQuery(id+"F12.imprint","IMPRINT",EDGE,{"derivedFrom":subQ7}),1.0]])]}),makeQuery(id+"F12.imprint","IMPRINT",FACE,{"disambiguationData":[TD([[makeQuery(id+"F12.imprint","IMPRINT",EDGE,{"derivedFrom":subQ14}),1.0]])]}),makeQuery(id+"F12.imprint","IMPRINT",FACE,{"disambiguationData":[TD([[makeQuery(id+"F12.imprint","IMPRINT",EDGE,{"derivedFrom":subQ16}),1.0]])]}),makeQuery(id+"F12.imprint","IMPRINT",FACE,{"disambiguationData":[TD([[makeQuery(id+"F12.imprint","IMPRINT",EDGE,{"derivedFrom":subQ18}),-1.0]])]})]);}
            var Q1;
            Q1=makeQuery(id+"F5.boolean.opBoolean","SPLIT",FACE,{"disambiguationData":[TD([makeQuery(id+"F5.opExtrude","SWEPT_FACE",FACE,{"disambiguationData":[OSD([sQuery(id+"F4.wireOp",EDGE,"E41")])]})])],"derivedFrom":makeQuery(id+"F3.boolean.opBoolean","COPY",FACE,{"derivedFrom":makeQuery(id+"F3.opExtrude","CAP_FACE",FACE,{"disambiguationData":[OSD([sQuery(id+"F0.wireOp",EDGE,"E25.0"),sQuery(id+"F0.wireOp",EDGE,"E25.1"),sQuery(id+"F0.wireOp",EDGE,"E25.2"),sQuery(id+"F0.wireOp",EDGE,"E25.3"),sQuery(id+"F0.wireOp",EDGE,"E25.4"),sQuery(id+"F0.wireOp",EDGE,"E25.5"),sQuery(id+"F0.wireOp",EDGE,"E25.6"),sQuery(id+"F0.wireOp",EDGE,"E25.7")])],"isStart":false})})});
            extrude(context, id + "F13", {"entities" : qUnion([Q0]), "operationType" : NewBodyOperationType.REMOVE, "endBound" : BoundingType.UP_TO_SURFACE, "endBoundEntityFace" : qUnion([Q1]), "depth" : 25 * mm});
        }
        {
            var Q0;
            Q0=makeQuery(id+"F3.boolean.opBoolean","COPY",EDGE,{"derivedFrom":makeQuery(id+"F3.opExtrude","CAP_EDGE",EDGE,{"disambiguationData":[OSD([sQuery(id+"F0.wireOp",EDGE,"E25.6")])],"isStart":false})});
            var Q1;
            Q1=makeQuery(id+"F8.boolean.opBoolean","INTERSECT",EDGE,{"derivedFrom":[makeQuery(id+"F5.opExtrude","SWEPT_FACE",FACE,{"disambiguationData":[OSD([sQuery(id+"F4.wireOp",EDGE,"E30")])]}),makeQuery(id+"F8.opExtrude","CAP_FACE",FACE,{"disambiguationData":[OSD([sQuery(id+"F7.wireOp",EDGE,"E67")])],"isStart":false})]});
            var Q2;
            Q2=makeQuery(id+"F8.boolean.opBoolean","INTERSECT",EDGE,{"disambiguationData":[OD(1.0)],"derivedFrom":[makeQuery(id+"F5.opExtrude","SWEPT_FACE",FACE,{"disambiguationData":[OSD([sQuery(id+"F4.wireOp",EDGE,"E30")])]}),makeQuery(id+"F8.opExtrude","SWEPT_FACE",FACE,{"disambiguationData":[OSD([sQuery(id+"F7.wireOp",EDGE,"E67")])]})]});
            var Q3;
            {var subQ0=sQuery(id+"F4.wireOp",EDGE,"E30");Q3=makeQuery(id+"F8.boolean.opBoolean","SPLIT",EDGE,{"disambiguationData":[TD([makeQuery(id+"F5.opExtrude","SWEPT_FACE",FACE,{"disambiguationData":[OSD([sQuery(id+"F4.wireOp",EDGE,"E35.filletArc")])]})])],"derivedFrom":makeQuery(id+"F5.opExtrude","CAP_EDGE",EDGE,{"disambiguationData":[OSD([subQ0])],"isStart":false})});}
            var Q4;
            {var subQ0=sQuery(id+"F0.wireOp",EDGE,"E25.7");var subQ1=sQuery(id+"F0.wireOp",EDGE,"E25.1");var subQ2=sQuery(id+"F0.wireOp",EDGE,"E25.6");var subQ3=sQuery(id+"F0.wireOp",EDGE,"E25.5");var subQ4=sQuery(id+"F0.wireOp",EDGE,"E25.4");var subQ5=sQuery(id+"F0.wireOp",EDGE,"E25.0");var subQ6=sQuery(id+"F0.wireOp",EDGE,"E25.2");var subQ7=sQuery(id+"F0.wireOp",EDGE,"E25.3");Q4=makeQuery(id+"F8.boolean.opBoolean","INTERSECT",EDGE,{"derivedFrom":[makeQuery(id+"F5.boolean.opBoolean","SPLIT",FACE,{"disambiguationData":[TD([makeQuery(id+"F2.opExtrude","SWEPT_FACE",FACE,{"disambiguationData":[OSD([subQ5])]})])],"derivedFrom":makeQuery(id+"F3.boolean.opBoolean","COPY",FACE,{"derivedFrom":makeQuery(id+"F3.opExtrude","CAP_FACE",FACE,{"disambiguationData":[OSD([subQ5,subQ1,subQ6,subQ7,subQ4,subQ3,subQ2,subQ0])],"isStart":false})})}),makeQuery(id+"F8.opExtrude","SWEPT_FACE",FACE,{"disambiguationData":[OSD([sQuery(id+"F7.wireOp",EDGE,"E67")])]})]});}
            var Q5;
            Q5=makeQuery(id+"F8.boolean.opBoolean","INTERSECT",EDGE,{"disambiguationData":[OD(0.0)],"derivedFrom":[makeQuery(id+"F5.opExtrude","SWEPT_FACE",FACE,{"disambiguationData":[OSD([sQuery(id+"F4.wireOp",EDGE,"E30")])]}),makeQuery(id+"F8.opExtrude","SWEPT_FACE",FACE,{"disambiguationData":[OSD([sQuery(id+"F7.wireOp",EDGE,"E67")])]})]});
            fillet(context, id + "F14", {"entities" : qUnion([Q0, Q1, Q2, Q3, Q4, Q5]), "radius" : 3 * mm, "tangentPropagation" : true, "allowEdgeOverflow" : false});
        }
        {
            var Q0;
            Q0=makeQuery(id+"F1.opExtrude","CAP_EDGE",EDGE,{"disambiguationData":[OSD([sQuery(id+"F0.wireOp",EDGE,"E1.bottom")])],"isStart":false});
            fillet(context, id + "F15", {"entities" : qUnion([Q0]), "radius" : 2 * mm, "tangentPropagation" : true, "allowEdgeOverflow" : false});
        }
        {
            var Q0;
            {var subQ0=sQuery(id+"F0.wireOp",EDGE,"E22.filletArc");var subQ1=sQuery(id+"F0.wireOp",EDGE,"E7");var subQ2=sQuery(id+"F0.wireOp",EDGE,"E6");var subQ3=sQuery(id+"F0.wireOp",EDGE,"E5");var subQ4=sQuery(id+"F0.wireOp",EDGE,"E4");var subQ5=sQuery(id+"F0.wireOp",EDGE,"E1.bottom");var subQ6=sQuery(id+"F0.wireOp",EDGE,"E21.filletArc");var subQ7=sQuery(id+"F0.wireOp",EDGE,"E1.top");var subQ8=sQuery(id+"F0.wireOp",EDGE,"E1.left");var subQ9=sQuery(id+"F0.wireOp",EDGE,"E1.right");var subQ10=sQuery(id+"F0.wireOp",EDGE,"E23.filletArc");var subQ11=sQuery(id+"F0.wireOp",EDGE,"E24.filletArc");Q0=makeQuery(id+"F2.boolean.opBoolean","SPLIT",FACE,{"disambiguationData":[TD([makeQuery(id+"F1.opExtrude","SWEPT_FACE",FACE,{"disambiguationData":[OSD([subQ5])]})])],"derivedFrom":makeQuery(id+"F1.opExtrude","CAP_FACE",FACE,{"disambiguationData":[OSD([subQ5,subQ7,subQ8,subQ9,subQ4,subQ3,subQ2,subQ1,subQ6,subQ0,subQ10,subQ11])],"isStart":true})});}
            var sketch = newSketch(context, id + "F16", { "sketchPlane" : qUnion([Q0])});
            skLineSegment(sketch, "E79", {"start": v(61.05, 208.38) * mm, "end": v(79.05, 226.38) * mm});
            skLineSegment(sketch, "E80", {"start": v(79.05, 226.38) * mm, "end": v(79.05, 238.38) * mm});
            skLineSegment(sketch, "E81", {"start": v(109.05, 238.38) * mm, "end": v(109.05, 226.38) * mm});
            skLineSegment(sketch, "E82", {"start": v(109.05, 226.38) * mm, "end": v(127.05, 208.38) * mm});
            skCircle(sketch, "E83", {"center": v(94.05, 238.38) * mm, "radius": 6 * mm});
            skArc(sketch, "E84", {"start": v(109.05, 238.38) * mm, "mid": v(94.05, 253.38) * mm, "end": v(79.05, 238.38) * mm});
            skLineSegment(sketch, "E85", {"start": v(94.05, 238.38) * mm, "end": v(94.05, 208.38) * mm, "construction": true});
            skLineSegment(sketch, "E86", {"start": v(14.05, 118.38) * mm, "end": v(174.05, 118.38) * mm, "construction": true});
            skLineSegment(sketch, "E87.MirrorCS", {"start": v(127.05, 208.38) * mm, "end": v(109.05, 226.38) * mm});
            skLineSegment(sketch, "E88.MirrorCS", {"start": v(79.05, 238.38) * mm, "end": v(79.05, 226.38) * mm});
            skArc(sketch, "E89.MirrorCS", {"start": v(79.05, 238.38) * mm, "mid": v(94.05, 253.38) * mm, "end": v(109.05, 238.38) * mm});
            skLineSegment(sketch, "E90.MirrorCS", {"start": v(79.05, 226.38) * mm, "end": v(61.05, 208.38) * mm});
            skLineSegment(sketch, "E91.MirrorCS", {"start": v(109.05, 226.38) * mm, "end": v(109.05, 238.38) * mm});
            skLineSegment(sketch, "E92.MirrorCS", {"start": v(174.05, 118.38) * mm, "end": v(14.05, 118.38) * mm, "construction": true});
            skLineSegment(sketch, "E93.MirrorCS", {"start": v(109.05, 10.38) * mm, "end": v(109.05, -1.62) * mm});
            skLineSegment(sketch, "E94.MirrorCS", {"start": v(127.05, 28.38) * mm, "end": v(109.05, 10.38) * mm});
            skLineSegment(sketch, "E95.MirrorCS", {"start": v(79.05, 10.38) * mm, "end": v(79.05, -1.62) * mm});
            skLineSegment(sketch, "E96.MirrorCS", {"start": v(79.05, 10.38) * mm, "end": v(61.05, 28.38) * mm});
            skArc(sketch, "E97.MirrorCS", {"start": v(109.05, -1.62) * mm, "mid": v(94.05, -16.62) * mm, "end": v(79.05, -1.62) * mm});
            skLineSegment(sketch, "E98", {"start": v(61.05, 208.38) * mm, "end": v(127.05, 208.38) * mm});
            skLineSegment(sketch, "E99", {"start": v(61.05, 28.38) * mm, "end": v(127.05, 28.38) * mm});
            skSolve(sketch);
        }
        {
            var Q0;
            Q0=makeQuery(id+"F16.imprint","IMPRINT",FACE,{"disambiguationData":[TD([[makeQuery(id+"F16.imprint","IMPRINT",EDGE,{"derivedFrom":sQuery(id+"F16.wireOp",EDGE,"E80")}),-1.0]])]});
            var Q1;
            Q1=makeQuery(id+"F16.imprint","IMPRINT",FACE,{"disambiguationData":[TD([[makeQuery(id+"F16.imprint","IMPRINT",EDGE,{"derivedFrom":sQuery(id+"F16.wireOp",EDGE,"E93.MirrorCS")}),-1.0]])]});
            var Q2;
            Q2=makeQuery(id+"F2.opExtrude","CAP_FACE",FACE,{"disambiguationData":[OSD([sQuery(id+"F0.wireOp",EDGE,"E12"),sQuery(id+"F0.wireOp",EDGE,"E13"),sQuery(id+"F0.wireOp",EDGE,"E14"),sQuery(id+"F0.wireOp",EDGE,"E15"),sQuery(id+"F0.wireOp",EDGE,"E17.filletArc"),sQuery(id+"F0.wireOp",EDGE,"E18.filletArc"),sQuery(id+"F0.wireOp",EDGE,"E19.filletArc"),sQuery(id+"F0.wireOp",EDGE,"E20.filletArc"),sQuery(id+"F0.wireOp",EDGE,"E25.0"),sQuery(id+"F0.wireOp",EDGE,"E25.1"),sQuery(id+"F0.wireOp",EDGE,"E25.2"),sQuery(id+"F0.wireOp",EDGE,"E25.3"),sQuery(id+"F0.wireOp",EDGE,"E25.4"),sQuery(id+"F0.wireOp",EDGE,"E25.5"),sQuery(id+"F0.wireOp",EDGE,"E25.6"),sQuery(id+"F0.wireOp",EDGE,"E25.7")])],"isStart":false});
            extrude(context, id + "F17", {"entities" : qUnion([Q0, Q1]), "endBound" : BoundingType.UP_TO_SURFACE, "endBoundEntityFace" : qUnion([Q2]), "depth" : 25 * mm});
        }
    });
